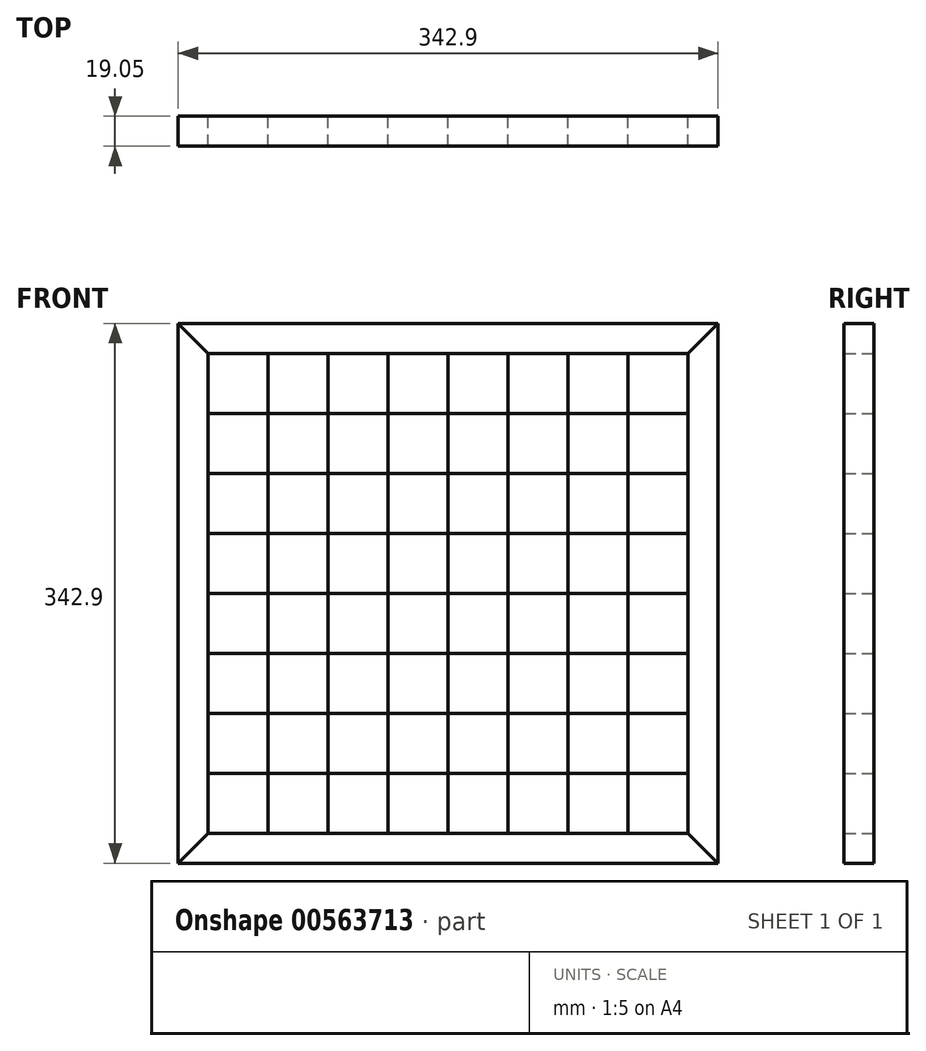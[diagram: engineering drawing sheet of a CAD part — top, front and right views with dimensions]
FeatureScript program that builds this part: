
annotation { "Feature Type Name" : "Feature", "Feature Type Description" : "" }
export const myFeature = defineFeature(function(context is Context, id is Id, definition is map)
    precondition{}
    {
        {
            var Q0;
            Q0=qCreatedBy(makeId("Front.planeOp"),FACE);
            var sketch = newSketch(context, id + "F0", { "sketchPlane" : qUnion([Q0])});
            skLineSegment(sketch, "E0.bottom", {"start": v(171.45, -171.45) * mm, "end": v(-171.45, -171.45) * mm});
            skLineSegment(sketch, "E0.top", {"start": v(171.45, 171.45) * mm, "end": v(-171.45, 171.45) * mm});
            skLineSegment(sketch, "E0.left", {"start": v(171.45, -171.45) * mm, "end": v(171.45, 171.45) * mm});
            skLineSegment(sketch, "E0.right", {"start": v(-171.45, -171.45) * mm, "end": v(-171.45, 171.45) * mm});
            skPoint(sketch, "E0.middle", {"position": v(0, 0) * mm});
            skSolve(sketch);
        }
        {
            var Q0;
            Q0=qCreatedBy(makeId("Front.planeOp"),FACE);
            var sketch = newSketch(context, id + "F1", { "sketchPlane" : qUnion([Q0])});
            skLineSegment(sketch, "E1.0.0", {"start": v(171.45, -171.45) * mm, "end": v(171.45, 171.45) * mm});
            skLineSegment(sketch, "E1.0.1", {"start": v(171.45, 171.45) * mm, "end": v(-171.45, 171.45) * mm});
            skLineSegment(sketch, "E1.0.2", {"start": v(-171.45, 171.45) * mm, "end": v(-171.45, -171.45) * mm});
            skLineSegment(sketch, "E1.0.3", {"start": v(-171.45, -171.45) * mm, "end": v(171.45, -171.45) * mm});
            skLineSegment(sketch, "E2", {"start": v(-171.45, 171.45) * mm, "end": v(-152.4, 152.4) * mm});
            skLineSegment(sketch, "E3", {"start": v(-152.4, 152.4) * mm, "end": v(-152.4, -152.4) * mm});
            skLineSegment(sketch, "E4", {"start": v(-152.4, -152.4) * mm, "end": v(-171.45, -171.45) * mm});
            skLineSegment(sketch, "E5", {"start": v(-152.4, 152.4) * mm, "end": v(152.4, 152.4) * mm});
            skLineSegment(sketch, "E6", {"start": v(152.4, 152.4) * mm, "end": v(171.45, 171.45) * mm});
            skLineSegment(sketch, "E7", {"start": v(-152.4, -152.4) * mm, "end": v(152.4, -152.4) * mm});
            skLineSegment(sketch, "E8", {"start": v(152.4, -152.4) * mm, "end": v(171.45, -171.45) * mm});
            skLineSegment(sketch, "E9", {"start": v(152.4, 152.4) * mm, "end": v(152.4, -152.4) * mm});
            skSolve(sketch);
        }
        {
            var Q0;
            Q0=makeQuery(id+"F1.imprint","IMPRINT",FACE,{"disambiguationData":[TD([[makeQuery(id+"F1.imprint","IMPRINT",EDGE,{"derivedFrom":sQuery(id+"F1.wireOp",EDGE,"E1.0.2")}),1.0]])]});
            extrude(context, id + "F2", {"entities" : qUnion([Q0]), "depth" : 19.05 * mm, "offsetDistance" : 25.4 * mm});
        }
        {
            var Q0;
            Q0=makeQuery(id+"F1.imprint","IMPRINT",FACE,{"disambiguationData":[TD([[makeQuery(id+"F1.imprint","IMPRINT",EDGE,{"derivedFrom":sQuery(id+"F1.wireOp",EDGE,"E1.0.3")}),1.0]])]});
            extrude(context, id + "F3", {"entities" : qUnion([Q0]), "depth" : 19.05 * mm, "offsetDistance" : 25.4 * mm});
        }
        {
            var Q0;
            Q0=makeQuery(id+"F1.imprint","IMPRINT",FACE,{"disambiguationData":[TD([[makeQuery(id+"F1.imprint","IMPRINT",EDGE,{"derivedFrom":sQuery(id+"F1.wireOp",EDGE,"E1.0.1")}),1.0]])]});
            extrude(context, id + "F4", {"entities" : qUnion([Q0]), "depth" : 19.05 * mm, "offsetDistance" : 25.4 * mm});
        }
        {
            var Q0;
            Q0=makeQuery(id+"F1.imprint","IMPRINT",FACE,{"disambiguationData":[TD([[makeQuery(id+"F1.imprint","IMPRINT",EDGE,{"derivedFrom":sQuery(id+"F1.wireOp",EDGE,"E1.0.0")}),1.0]])]});
            extrude(context, id + "F5", {"entities" : qUnion([Q0]), "depth" : 19.05 * mm, "offsetDistance" : 25.4 * mm});
        }
        {
            var Q0;
            Q0=qCreatedBy(makeId("Front.planeOp"),FACE);
            var sketch = newSketch(context, id + "F6", { "sketchPlane" : qUnion([Q0])});
            skLineSegment(sketch, "E10.0", {"start": v(-152.4, 152.4) * mm, "end": v(152.4, 152.4) * mm});
            skLineSegment(sketch, "E11.0", {"start": v(-152.4, 152.4) * mm, "end": v(-152.4, -152.4) * mm});
            skLineSegment(sketch, "E12.0", {"start": v(-152.4, -152.4) * mm, "end": v(152.4, -152.4) * mm});
            skLineSegment(sketch, "E13.0", {"start": v(152.4, 152.4) * mm, "end": v(152.4, -152.4) * mm});
            skLineSegment(sketch, "E14", {"start": v(-152.4, 114.3) * mm, "end": v(152.4, 114.3) * mm});
            skLineSegment(sketch, "E15", {"start": v(-152.4, 76.2) * mm, "end": v(152.4, 76.2) * mm});
            skLineSegment(sketch, "E16", {"start": v(-152.4, 38.1) * mm, "end": v(152.4, 38.1) * mm});
            skLineSegment(sketch, "E17", {"start": v(-152.4, 0) * mm, "end": v(152.4, 0) * mm});
            skLineSegment(sketch, "E18", {"start": v(-152.4, -38.1) * mm, "end": v(152.4, -38.1) * mm});
            skLineSegment(sketch, "E19", {"start": v(-152.4, -76.2) * mm, "end": v(152.4, -76.2) * mm});
            skLineSegment(sketch, "E20", {"start": v(-152.4, -114.3) * mm, "end": v(152.4, -114.3) * mm});
            skLineSegment(sketch, "E21", {"start": v(-114.3, 152.4) * mm, "end": v(-114.3, -152.4) * mm});
            skLineSegment(sketch, "E22", {"start": v(-76.2, 152.4) * mm, "end": v(-76.2, -152.4) * mm});
            skLineSegment(sketch, "E23", {"start": v(-38.1, 152.4) * mm, "end": v(-38.1, -152.4) * mm});
            skLineSegment(sketch, "E24", {"start": v(38.1, 152.4) * mm, "end": v(38.1, -152.4) * mm});
            skLineSegment(sketch, "E25", {"start": v(114.3, 152.4) * mm, "end": v(114.3, -152.4) * mm});
            skLineSegment(sketch, "E26", {"start": v(76.2, 152.4) * mm, "end": v(76.2, -152.4) * mm});
            skLineSegment(sketch, "E27", {"start": v(0, 152.4) * mm, "end": v(0, -152.4) * mm});
            skSolve(sketch);
        }
        {
            var Q0;
            {var subQ0=sQuery(id+"F6.wireOp",EDGE,"E11.0");var subQ1=sQuery(id+"F6.wireOp",EDGE,"E10.0");var subQ2=makeQuery(id+"F6.imprint","INTERSECT",VERTEX,{"derivedFrom":[subQ1,subQ0]});Q0=makeQuery(id+"F6.imprint","IMPRINT",FACE,{"disambiguationData":[TD([[makeQuery(id+"F6.imprint","IMPRINT",EDGE,{"disambiguationData":[TD([[subQ2,-1.0]])],"derivedFrom":subQ1}),-1.0]])]});}
            var Q1;
            {var subQ0=sQuery(id+"F6.wireOp",EDGE,"E15");var subQ1=sQuery(id+"F6.wireOp",EDGE,"E11.0");var subQ2=makeQuery(id+"F6.imprint","INTERSECT",VERTEX,{"derivedFrom":[subQ1,subQ0]});Q1=makeQuery(id+"F6.imprint","IMPRINT",FACE,{"disambiguationData":[TD([[makeQuery(id+"F6.imprint","IMPRINT",EDGE,{"disambiguationData":[TD([[subQ2,-1.0]])],"derivedFrom":subQ1}),1.0]])]});}
            var Q2;
            {var subQ0=sQuery(id+"F6.wireOp",EDGE,"E17");var subQ1=sQuery(id+"F6.wireOp",EDGE,"E11.0");var subQ2=makeQuery(id+"F6.imprint","INTERSECT",VERTEX,{"derivedFrom":[subQ1,subQ0]});Q2=makeQuery(id+"F6.imprint","IMPRINT",FACE,{"disambiguationData":[TD([[makeQuery(id+"F6.imprint","IMPRINT",EDGE,{"disambiguationData":[TD([[subQ2,-1.0]])],"derivedFrom":subQ1}),1.0]])]});}
            var Q3;
            {var subQ0=sQuery(id+"F6.wireOp",EDGE,"E19");var subQ1=sQuery(id+"F6.wireOp",EDGE,"E11.0");var subQ2=makeQuery(id+"F6.imprint","INTERSECT",VERTEX,{"derivedFrom":[subQ1,subQ0]});Q3=makeQuery(id+"F6.imprint","IMPRINT",FACE,{"disambiguationData":[TD([[makeQuery(id+"F6.imprint","IMPRINT",EDGE,{"disambiguationData":[TD([[subQ2,-1.0]])],"derivedFrom":subQ1}),1.0]])]});}
            var Q4;
            {var subQ0=sQuery(id+"F6.wireOp",EDGE,"E21");var subQ1=sQuery(id+"F6.wireOp",EDGE,"E12.0");var subQ2=makeQuery(id+"F6.imprint","INTERSECT",VERTEX,{"derivedFrom":[subQ1,subQ0]});Q4=makeQuery(id+"F6.imprint","IMPRINT",FACE,{"disambiguationData":[TD([[makeQuery(id+"F6.imprint","IMPRINT",EDGE,{"disambiguationData":[TD([[subQ2,-1.0]])],"derivedFrom":subQ1}),1.0]])]});}
            var Q5;
            {var subQ0=sQuery(id+"F6.wireOp",EDGE,"E21");var subQ1=sQuery(id+"F6.wireOp",EDGE,"E18");var subQ2=makeQuery(id+"F6.imprint","INTERSECT",VERTEX,{"derivedFrom":[subQ1,subQ0]});Q5=makeQuery(id+"F6.imprint","IMPRINT",FACE,{"disambiguationData":[TD([[makeQuery(id+"F6.imprint","IMPRINT",EDGE,{"disambiguationData":[TD([[subQ2,-1.0]])],"derivedFrom":subQ1}),-1.0]])]});}
            var Q6;
            {var subQ0=sQuery(id+"F6.wireOp",EDGE,"E21");var subQ1=sQuery(id+"F6.wireOp",EDGE,"E16");var subQ2=makeQuery(id+"F6.imprint","INTERSECT",VERTEX,{"derivedFrom":[subQ1,subQ0]});Q6=makeQuery(id+"F6.imprint","IMPRINT",FACE,{"disambiguationData":[TD([[makeQuery(id+"F6.imprint","IMPRINT",EDGE,{"disambiguationData":[TD([[subQ2,-1.0]])],"derivedFrom":subQ1}),-1.0]])]});}
            var Q7;
            {var subQ0=sQuery(id+"F6.wireOp",EDGE,"E21");var subQ1=sQuery(id+"F6.wireOp",EDGE,"E14");var subQ2=makeQuery(id+"F6.imprint","INTERSECT",VERTEX,{"derivedFrom":[subQ1,subQ0]});Q7=makeQuery(id+"F6.imprint","IMPRINT",FACE,{"disambiguationData":[TD([[makeQuery(id+"F6.imprint","IMPRINT",EDGE,{"disambiguationData":[TD([[subQ2,-1.0]])],"derivedFrom":subQ1}),-1.0]])]});}
            var Q8;
            {var subQ0=sQuery(id+"F6.wireOp",EDGE,"E22");var subQ1=sQuery(id+"F6.wireOp",EDGE,"E10.0");var subQ2=makeQuery(id+"F6.imprint","INTERSECT",VERTEX,{"derivedFrom":[subQ1,subQ0]});Q8=makeQuery(id+"F6.imprint","IMPRINT",FACE,{"disambiguationData":[TD([[makeQuery(id+"F6.imprint","IMPRINT",EDGE,{"disambiguationData":[TD([[subQ2,-1.0]])],"derivedFrom":subQ1}),-1.0]])]});}
            var Q9;
            {var subQ0=sQuery(id+"F6.wireOp",EDGE,"E22");var subQ1=sQuery(id+"F6.wireOp",EDGE,"E15");var subQ2=makeQuery(id+"F6.imprint","INTERSECT",VERTEX,{"derivedFrom":[subQ1,subQ0]});Q9=makeQuery(id+"F6.imprint","IMPRINT",FACE,{"disambiguationData":[TD([[makeQuery(id+"F6.imprint","IMPRINT",EDGE,{"disambiguationData":[TD([[subQ2,-1.0]])],"derivedFrom":subQ1}),-1.0]])]});}
            var Q10;
            {var subQ0=sQuery(id+"F6.wireOp",EDGE,"E22");var subQ1=sQuery(id+"F6.wireOp",EDGE,"E17");var subQ2=makeQuery(id+"F6.imprint","INTERSECT",VERTEX,{"derivedFrom":[subQ1,subQ0]});Q10=makeQuery(id+"F6.imprint","IMPRINT",FACE,{"disambiguationData":[TD([[makeQuery(id+"F6.imprint","IMPRINT",EDGE,{"disambiguationData":[TD([[subQ2,-1.0]])],"derivedFrom":subQ1}),-1.0]])]});}
            var Q11;
            {var subQ0=sQuery(id+"F6.wireOp",EDGE,"E22");var subQ1=sQuery(id+"F6.wireOp",EDGE,"E19");var subQ2=makeQuery(id+"F6.imprint","INTERSECT",VERTEX,{"derivedFrom":[subQ1,subQ0]});Q11=makeQuery(id+"F6.imprint","IMPRINT",FACE,{"disambiguationData":[TD([[makeQuery(id+"F6.imprint","IMPRINT",EDGE,{"disambiguationData":[TD([[subQ2,-1.0]])],"derivedFrom":subQ1}),-1.0]])]});}
            var Q12;
            {var subQ0=sQuery(id+"F6.wireOp",EDGE,"E23");var subQ1=sQuery(id+"F6.wireOp",EDGE,"E12.0");var subQ2=makeQuery(id+"F6.imprint","INTERSECT",VERTEX,{"derivedFrom":[subQ1,subQ0]});Q12=makeQuery(id+"F6.imprint","IMPRINT",FACE,{"disambiguationData":[TD([[makeQuery(id+"F6.imprint","IMPRINT",EDGE,{"disambiguationData":[TD([[subQ2,-1.0]])],"derivedFrom":subQ1}),1.0]])]});}
            var Q13;
            {var subQ0=sQuery(id+"F6.wireOp",EDGE,"E23");var subQ1=sQuery(id+"F6.wireOp",EDGE,"E18");var subQ2=makeQuery(id+"F6.imprint","INTERSECT",VERTEX,{"derivedFrom":[subQ1,subQ0]});Q13=makeQuery(id+"F6.imprint","IMPRINT",FACE,{"disambiguationData":[TD([[makeQuery(id+"F6.imprint","IMPRINT",EDGE,{"disambiguationData":[TD([[subQ2,-1.0]])],"derivedFrom":subQ1}),-1.0]])]});}
            var Q14;
            {var subQ0=sQuery(id+"F6.wireOp",EDGE,"E23");var subQ1=sQuery(id+"F6.wireOp",EDGE,"E16");var subQ2=makeQuery(id+"F6.imprint","INTERSECT",VERTEX,{"derivedFrom":[subQ1,subQ0]});Q14=makeQuery(id+"F6.imprint","IMPRINT",FACE,{"disambiguationData":[TD([[makeQuery(id+"F6.imprint","IMPRINT",EDGE,{"disambiguationData":[TD([[subQ2,-1.0]])],"derivedFrom":subQ1}),-1.0]])]});}
            var Q15;
            {var subQ0=sQuery(id+"F6.wireOp",EDGE,"E23");var subQ1=sQuery(id+"F6.wireOp",EDGE,"E14");var subQ2=makeQuery(id+"F6.imprint","INTERSECT",VERTEX,{"derivedFrom":[subQ1,subQ0]});Q15=makeQuery(id+"F6.imprint","IMPRINT",FACE,{"disambiguationData":[TD([[makeQuery(id+"F6.imprint","IMPRINT",EDGE,{"disambiguationData":[TD([[subQ2,-1.0]])],"derivedFrom":subQ1}),-1.0]])]});}
            var Q16;
            {var subQ0=sQuery(id+"F6.wireOp",EDGE,"E24");var subQ1=sQuery(id+"F6.wireOp",EDGE,"E10.0");var subQ2=makeQuery(id+"F6.imprint","INTERSECT",VERTEX,{"derivedFrom":[subQ1,subQ0]});Q16=makeQuery(id+"F6.imprint","IMPRINT",FACE,{"disambiguationData":[TD([[makeQuery(id+"F6.imprint","IMPRINT",EDGE,{"disambiguationData":[TD([[subQ2,1.0]])],"derivedFrom":subQ1}),-1.0]])]});}
            var Q17;
            {var subQ0=sQuery(id+"F6.wireOp",EDGE,"E27");var subQ1=sQuery(id+"F6.wireOp",EDGE,"E15");var subQ2=makeQuery(id+"F6.imprint","INTERSECT",VERTEX,{"derivedFrom":[subQ1,subQ0]});Q17=makeQuery(id+"F6.imprint","IMPRINT",FACE,{"disambiguationData":[TD([[makeQuery(id+"F6.imprint","IMPRINT",EDGE,{"disambiguationData":[TD([[subQ2,-1.0]])],"derivedFrom":subQ1}),-1.0]])]});}
            var Q18;
            {var subQ0=sQuery(id+"F6.wireOp",EDGE,"E24");var subQ1=sQuery(id+"F6.wireOp",EDGE,"E18");var subQ2=makeQuery(id+"F6.imprint","INTERSECT",VERTEX,{"derivedFrom":[subQ1,subQ0]});Q18=makeQuery(id+"F6.imprint","IMPRINT",FACE,{"disambiguationData":[TD([[makeQuery(id+"F6.imprint","IMPRINT",EDGE,{"disambiguationData":[TD([[subQ2,-1.0]])],"derivedFrom":subQ1}),-1.0]])]});}
            var Q19;
            {var subQ0=sQuery(id+"F6.wireOp",EDGE,"E24");var subQ1=sQuery(id+"F6.wireOp",EDGE,"E16");var subQ2=makeQuery(id+"F6.imprint","INTERSECT",VERTEX,{"derivedFrom":[subQ1,subQ0]});Q19=makeQuery(id+"F6.imprint","IMPRINT",FACE,{"disambiguationData":[TD([[makeQuery(id+"F6.imprint","IMPRINT",EDGE,{"disambiguationData":[TD([[subQ2,-1.0]])],"derivedFrom":subQ1}),-1.0]])]});}
            var Q20;
            {var subQ0=sQuery(id+"F6.wireOp",EDGE,"E24");var subQ1=sQuery(id+"F6.wireOp",EDGE,"E14");var subQ2=makeQuery(id+"F6.imprint","INTERSECT",VERTEX,{"derivedFrom":[subQ1,subQ0]});Q20=makeQuery(id+"F6.imprint","IMPRINT",FACE,{"disambiguationData":[TD([[makeQuery(id+"F6.imprint","IMPRINT",EDGE,{"disambiguationData":[TD([[subQ2,-1.0]])],"derivedFrom":subQ1}),-1.0]])]});}
            var Q21;
            {var subQ0=sQuery(id+"F6.wireOp",EDGE,"E27");var subQ1=sQuery(id+"F6.wireOp",EDGE,"E19");var subQ2=makeQuery(id+"F6.imprint","INTERSECT",VERTEX,{"derivedFrom":[subQ1,subQ0]});Q21=makeQuery(id+"F6.imprint","IMPRINT",FACE,{"disambiguationData":[TD([[makeQuery(id+"F6.imprint","IMPRINT",EDGE,{"disambiguationData":[TD([[subQ2,-1.0]])],"derivedFrom":subQ1}),-1.0]])]});}
            var Q22;
            {var subQ0=sQuery(id+"F6.wireOp",EDGE,"E27");var subQ1=sQuery(id+"F6.wireOp",EDGE,"E17");var subQ2=makeQuery(id+"F6.imprint","INTERSECT",VERTEX,{"derivedFrom":[subQ1,subQ0]});Q22=makeQuery(id+"F6.imprint","IMPRINT",FACE,{"disambiguationData":[TD([[makeQuery(id+"F6.imprint","IMPRINT",EDGE,{"disambiguationData":[TD([[subQ2,-1.0]])],"derivedFrom":subQ1}),-1.0]])]});}
            var Q23;
            {var subQ0=sQuery(id+"F6.wireOp",EDGE,"E26");var subQ1=sQuery(id+"F6.wireOp",EDGE,"E19");var subQ2=makeQuery(id+"F6.imprint","INTERSECT",VERTEX,{"derivedFrom":[subQ1,subQ0]});Q23=makeQuery(id+"F6.imprint","IMPRINT",FACE,{"disambiguationData":[TD([[makeQuery(id+"F6.imprint","IMPRINT",EDGE,{"disambiguationData":[TD([[subQ2,-1.0]])],"derivedFrom":subQ1}),-1.0]])]});}
            var Q24;
            {var subQ0=sQuery(id+"F6.wireOp",EDGE,"E26");var subQ1=sQuery(id+"F6.wireOp",EDGE,"E17");var subQ2=makeQuery(id+"F6.imprint","INTERSECT",VERTEX,{"derivedFrom":[subQ1,subQ0]});Q24=makeQuery(id+"F6.imprint","IMPRINT",FACE,{"disambiguationData":[TD([[makeQuery(id+"F6.imprint","IMPRINT",EDGE,{"disambiguationData":[TD([[subQ2,-1.0]])],"derivedFrom":subQ1}),-1.0]])]});}
            var Q25;
            {var subQ0=sQuery(id+"F6.wireOp",EDGE,"E26");var subQ1=sQuery(id+"F6.wireOp",EDGE,"E15");var subQ2=makeQuery(id+"F6.imprint","INTERSECT",VERTEX,{"derivedFrom":[subQ1,subQ0]});Q25=makeQuery(id+"F6.imprint","IMPRINT",FACE,{"disambiguationData":[TD([[makeQuery(id+"F6.imprint","IMPRINT",EDGE,{"disambiguationData":[TD([[subQ2,-1.0]])],"derivedFrom":subQ1}),-1.0]])]});}
            var Q26;
            {var subQ0=sQuery(id+"F6.wireOp",EDGE,"E25");var subQ1=sQuery(id+"F6.wireOp",EDGE,"E10.0");var subQ2=makeQuery(id+"F6.imprint","INTERSECT",VERTEX,{"derivedFrom":[subQ1,subQ0]});Q26=makeQuery(id+"F6.imprint","IMPRINT",FACE,{"disambiguationData":[TD([[makeQuery(id+"F6.imprint","IMPRINT",EDGE,{"disambiguationData":[TD([[subQ2,1.0]])],"derivedFrom":subQ1}),-1.0]])]});}
            var Q27;
            {var subQ0=sQuery(id+"F6.wireOp",EDGE,"E14");var subQ1=sQuery(id+"F6.wireOp",EDGE,"E13.0");var subQ2=makeQuery(id+"F6.imprint","INTERSECT",VERTEX,{"derivedFrom":[subQ1,subQ0]});Q27=makeQuery(id+"F6.imprint","IMPRINT",FACE,{"disambiguationData":[TD([[makeQuery(id+"F6.imprint","IMPRINT",EDGE,{"disambiguationData":[TD([[subQ2,-1.0]])],"derivedFrom":subQ1}),-1.0]])]});}
            var Q28;
            {var subQ0=sQuery(id+"F6.wireOp",EDGE,"E16");var subQ1=sQuery(id+"F6.wireOp",EDGE,"E13.0");var subQ2=makeQuery(id+"F6.imprint","INTERSECT",VERTEX,{"derivedFrom":[subQ1,subQ0]});Q28=makeQuery(id+"F6.imprint","IMPRINT",FACE,{"disambiguationData":[TD([[makeQuery(id+"F6.imprint","IMPRINT",EDGE,{"disambiguationData":[TD([[subQ2,-1.0]])],"derivedFrom":subQ1}),-1.0]])]});}
            var Q29;
            {var subQ0=sQuery(id+"F6.wireOp",EDGE,"E18");var subQ1=sQuery(id+"F6.wireOp",EDGE,"E13.0");var subQ2=makeQuery(id+"F6.imprint","INTERSECT",VERTEX,{"derivedFrom":[subQ1,subQ0]});Q29=makeQuery(id+"F6.imprint","IMPRINT",FACE,{"disambiguationData":[TD([[makeQuery(id+"F6.imprint","IMPRINT",EDGE,{"disambiguationData":[TD([[subQ2,-1.0]])],"derivedFrom":subQ1}),-1.0]])]});}
            var Q30;
            {var subQ0=sQuery(id+"F6.wireOp",EDGE,"E24");var subQ1=sQuery(id+"F6.wireOp",EDGE,"E12.0");var subQ2=makeQuery(id+"F6.imprint","INTERSECT",VERTEX,{"derivedFrom":[subQ1,subQ0]});Q30=makeQuery(id+"F6.imprint","IMPRINT",FACE,{"disambiguationData":[TD([[makeQuery(id+"F6.imprint","IMPRINT",EDGE,{"disambiguationData":[TD([[subQ2,-1.0]])],"derivedFrom":subQ1}),1.0]])]});}
            var Q31;
            {var subQ0=sQuery(id+"F6.wireOp",EDGE,"E13.0");var subQ1=sQuery(id+"F6.wireOp",EDGE,"E12.0");var subQ2=makeQuery(id+"F6.imprint","INTERSECT",VERTEX,{"derivedFrom":[subQ1,subQ0]});Q31=makeQuery(id+"F6.imprint","IMPRINT",FACE,{"disambiguationData":[TD([[makeQuery(id+"F6.imprint","IMPRINT",EDGE,{"disambiguationData":[TD([[subQ2,1.0]])],"derivedFrom":subQ1}),1.0]])]});}
            extrude(context, id + "F7", {"entities" : qUnion([Q0, Q1, Q2, Q3, Q4, Q5, Q6, Q7, Q8, Q9, Q10, Q11, Q12, Q13, Q14, Q15, Q16, Q17, Q18, Q19, Q20, Q21, Q22, Q23, Q24, Q25, Q26, Q27, Q28, Q29, Q30, Q31]), "depth" : 19.05 * mm, "offsetDistance" : 25.4 * mm});
        }
    });
